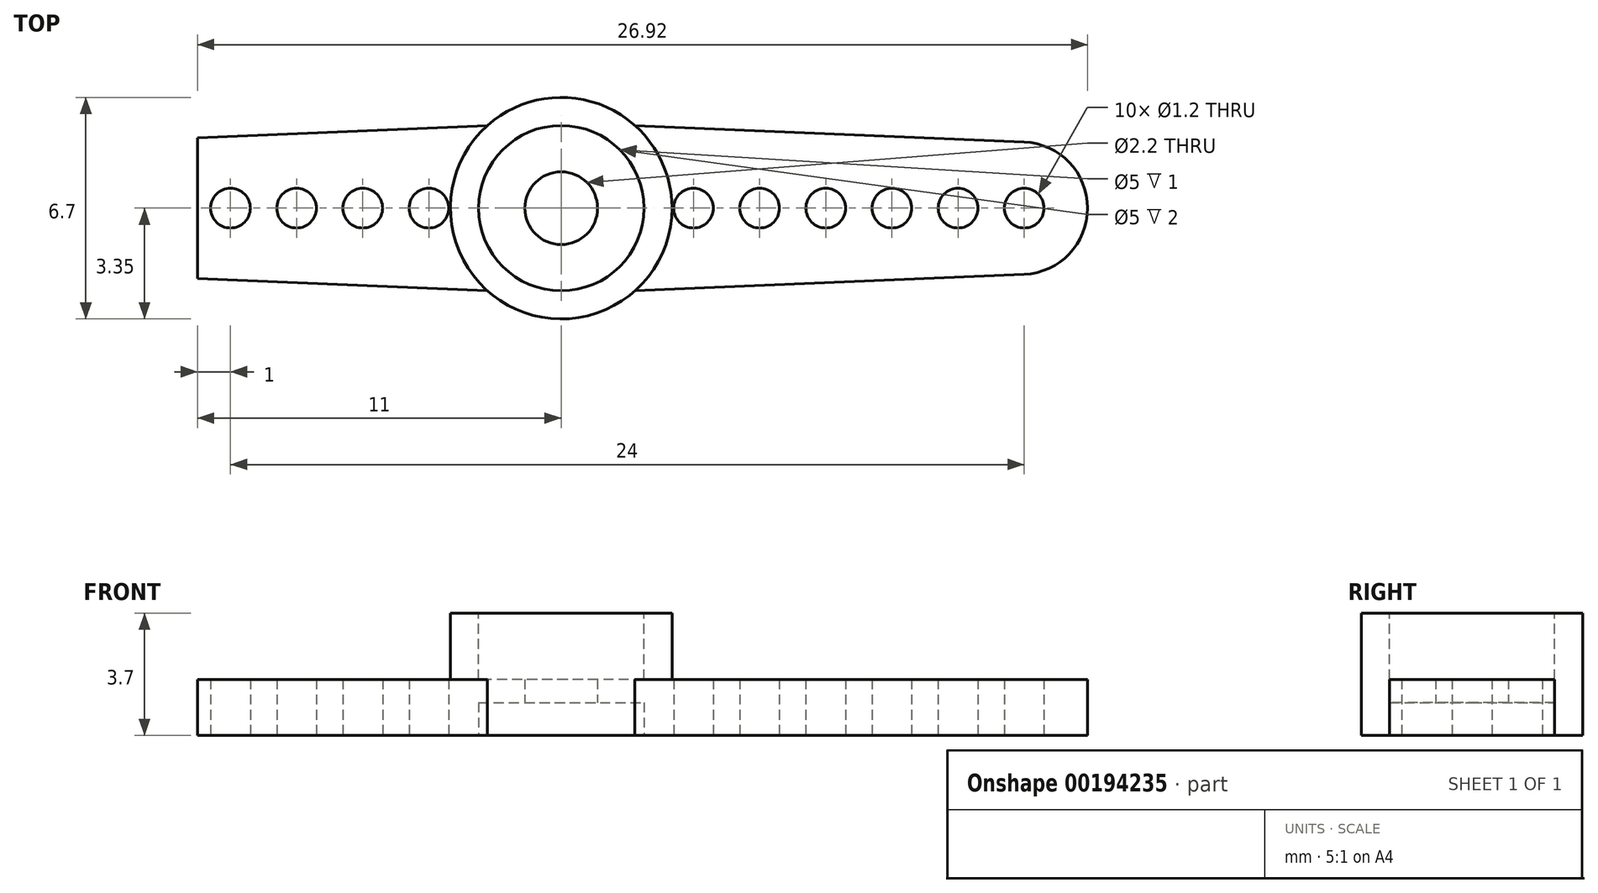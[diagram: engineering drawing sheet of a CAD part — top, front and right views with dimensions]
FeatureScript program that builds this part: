
annotation { "Feature Type Name" : "Feature", "Feature Type Description" : "" }
export const myFeature = defineFeature(function(context is Context, id is Id, definition is map)
    precondition{}
    {
        {
            var Q0;
            Q0=qCreatedBy(makeId("Top.planeOp"),FACE);
            var sketch = newSketch(context, id + "F0", { "sketchPlane" : qUnion([Q0])});
            skCircle(sketch, "E0", {"center": v(0, 0) * mm, "radius": 3.35 * mm});
            skLineSegment(sketch, "E1", {"start": v(0, 0) * mm, "end": v(-2.56, 0) * mm, "construction": true});
            skLineSegment(sketch, "E2", {"start": v(0, 0) * mm, "end": v(6, 0) * mm, "construction": true});
            skCircle(sketch, "E3", {"center": v(6, 0) * mm, "radius": 0.6 * mm});
            skCircle(sketch, "E4.1.0.0", {"center": v(8, 0) * mm, "radius": 0.6 * mm});
            skCircle(sketch, "E4.2.0.0", {"center": v(10, 0) * mm, "radius": 0.6 * mm});
            skCircle(sketch, "E4.3.0.0", {"center": v(12, 0) * mm, "radius": 0.6 * mm});
            skCircle(sketch, "E4.4.0.0", {"center": v(14, 0) * mm, "radius": 0.6 * mm});
            skLineSegment(sketch, "E4.direction1", {"start": v(6, 0) * mm, "end": v(8, 0) * mm, "construction": true});
            skCircle(sketch, "E5.1.0.0", {"center": v(4, 0) * mm, "radius": 0.6 * mm});
            skLineSegment(sketch, "E5.direction1", {"start": v(6, 0) * mm, "end": v(4, 0) * mm, "construction": true});
            skLineSegment(sketch, "E6", {"start": v(14, 2) * mm, "end": v(2.23, 2.5) * mm});
            skLineSegment(sketch, "E7.MirrorCS", {"start": v(14, -2) * mm, "end": v(2.23, -2.5) * mm});
            skArc(sketch, "E8", {"start": v(14, 2) * mm, "mid": v(15.92, 0) * mm, "end": v(14, -2) * mm});
            skLineSegment(sketch, "E9", {"start": v(0, 5) * mm, "end": v(0, -4.95) * mm, "construction": true});
            skCircle(sketch, "E10.MirrorC", {"center": v(-4, 0) * mm, "radius": 0.6 * mm});
            skCircle(sketch, "E11.MirrorC", {"center": v(-6, 0) * mm, "radius": 0.6 * mm});
            skCircle(sketch, "E12.MirrorC", {"center": v(-8, 0) * mm, "radius": 0.6 * mm});
            skCircle(sketch, "E13.MirrorC", {"center": v(-10, 0) * mm, "radius": 0.6 * mm});
            skLineSegment(sketch, "E14", {"start": v(-11, 2.13) * mm, "end": v(-11, -2.13) * mm});
            skLineSegment(sketch, "E15", {"start": v(-2.23, 2.5) * mm, "end": v(-11, 2.13) * mm});
            skLineSegment(sketch, "E16", {"start": v(-2.23, -2.5) * mm, "end": v(-11, -2.13) * mm});
            skSolve(sketch);
        }
        {
            var Q0;
            Q0=qSketchRegion(id+"F0",true);
            extrude(context, id + "F1", {"entities" : qUnion([Q0]), "depth" : 1.7 * mm});
        }
        {
            var Q0;
            Q0=makeQuery(id+"F1.opExtrude","CAP_FACE",FACE,{"disambiguationData":[OSD([sQuery(id+"F0.wireOp",EDGE,"E0"),sQuery(id+"F0.wireOp",EDGE,"E3"),sQuery(id+"F0.wireOp",EDGE,"E4.1.0.0"),sQuery(id+"F0.wireOp",EDGE,"E4.2.0.0"),sQuery(id+"F0.wireOp",EDGE,"E4.3.0.0"),sQuery(id+"F0.wireOp",EDGE,"E4.4.0.0"),sQuery(id+"F0.wireOp",EDGE,"E5.1.0.0"),sQuery(id+"F0.wireOp",EDGE,"E6"),sQuery(id+"F0.wireOp",EDGE,"E7.MirrorCS"),sQuery(id+"F0.wireOp",EDGE,"E8")])],"isStart":false});
            var sketch = newSketch(context, id + "F2", { "sketchPlane" : qUnion([Q0])});
            skCircle(sketch, "E17", {"center": v(0, 0) * mm, "radius": 3.35 * mm});
            skPoint(sketch, "E17.first.point", {"position": v(2.23, 2.5) * mm});
            skPoint(sketch, "E17.second.point", {"position": v(2.23, -2.5) * mm});
            skPoint(sketch, "E17.third.point", {"position": v(-3.35, 0.14) * mm});
            skSolve(sketch);
        }
        {
            var Q0;
            Q0=qSketchRegion(id+"F2",true);
            extrude(context, id + "F3", {"entities" : qUnion([Q0]), "operationType" : NewBodyOperationType.ADD, "depth" : 2 * mm});
        }
        {
            var Q0;
            Q0=makeQuery(id+"F1.opExtrude","CAP_FACE",FACE,{"disambiguationData":[OSD([sQuery(id+"F0.wireOp",EDGE,"E0"),sQuery(id+"F0.wireOp",EDGE,"E3"),sQuery(id+"F0.wireOp",EDGE,"E4.1.0.0"),sQuery(id+"F0.wireOp",EDGE,"E4.2.0.0"),sQuery(id+"F0.wireOp",EDGE,"E4.3.0.0"),sQuery(id+"F0.wireOp",EDGE,"E4.4.0.0"),sQuery(id+"F0.wireOp",EDGE,"E5.1.0.0"),sQuery(id+"F0.wireOp",EDGE,"E6"),sQuery(id+"F0.wireOp",EDGE,"E7.MirrorCS"),sQuery(id+"F0.wireOp",EDGE,"E8")])],"isStart":true});
            var sketch = newSketch(context, id + "F4", { "sketchPlane" : qUnion([Q0])});
            skCircle(sketch, "E18", {"center": v(0, 0) * mm, "radius": 2.5 * mm});
            skSolve(sketch);
        }
        {
            var Q0;
            Q0=qSketchRegion(id+"F4",true);
            extrude(context, id + "F5", {"entities" : qUnion([Q0]), "operationType" : NewBodyOperationType.REMOVE, "oppositeDirection" : true, "depth" : 1 * mm});
        }
        {
            var Q0;
            Q0=makeQuery(id+"F5.boolean.opBoolean","COPY",FACE,{"derivedFrom":makeQuery(id+"F5.opExtrude","CAP_FACE",FACE,{"disambiguationData":[OSD([sQuery(id+"F4.wireOp",EDGE,"E18")])],"isStart":false})});
            var sketch = newSketch(context, id + "F6", { "sketchPlane" : qUnion([Q0])});
            skCircle(sketch, "E19", {"center": v(0, 0) * mm, "radius": 1.1 * mm});
            skSolve(sketch);
        }
        {
            var Q0;
            Q0=qSketchRegion(id+"F6",true);
            extrude(context, id + "F7", {"entities" : qUnion([Q0]), "operationType" : NewBodyOperationType.REMOVE, "endBound" : BoundingType.THROUGH_ALL, "oppositeDirection" : true, "depth" : 1 * mm});
        }
        {
            var Q0;
            Q0=makeQuery(id+"F3.opExtrude","CAP_FACE",FACE,{"disambiguationData":[OSD([sQuery(id+"F2.wireOp",EDGE,"E17")])],"isStart":false});
            var sketch = newSketch(context, id + "F8", { "sketchPlane" : qUnion([Q0])});
            skCircle(sketch, "E20", {"center": v(0, 0) * mm, "radius": 2.5 * mm});
            skSolve(sketch);
        }
        {
            var Q0;
            Q0=qSketchRegion(id+"F8",true);
            extrude(context, id + "F9", {"entities" : qUnion([Q0]), "operationType" : NewBodyOperationType.REMOVE, "oppositeDirection" : true, "depth" : 2 * mm});
        }
    });
